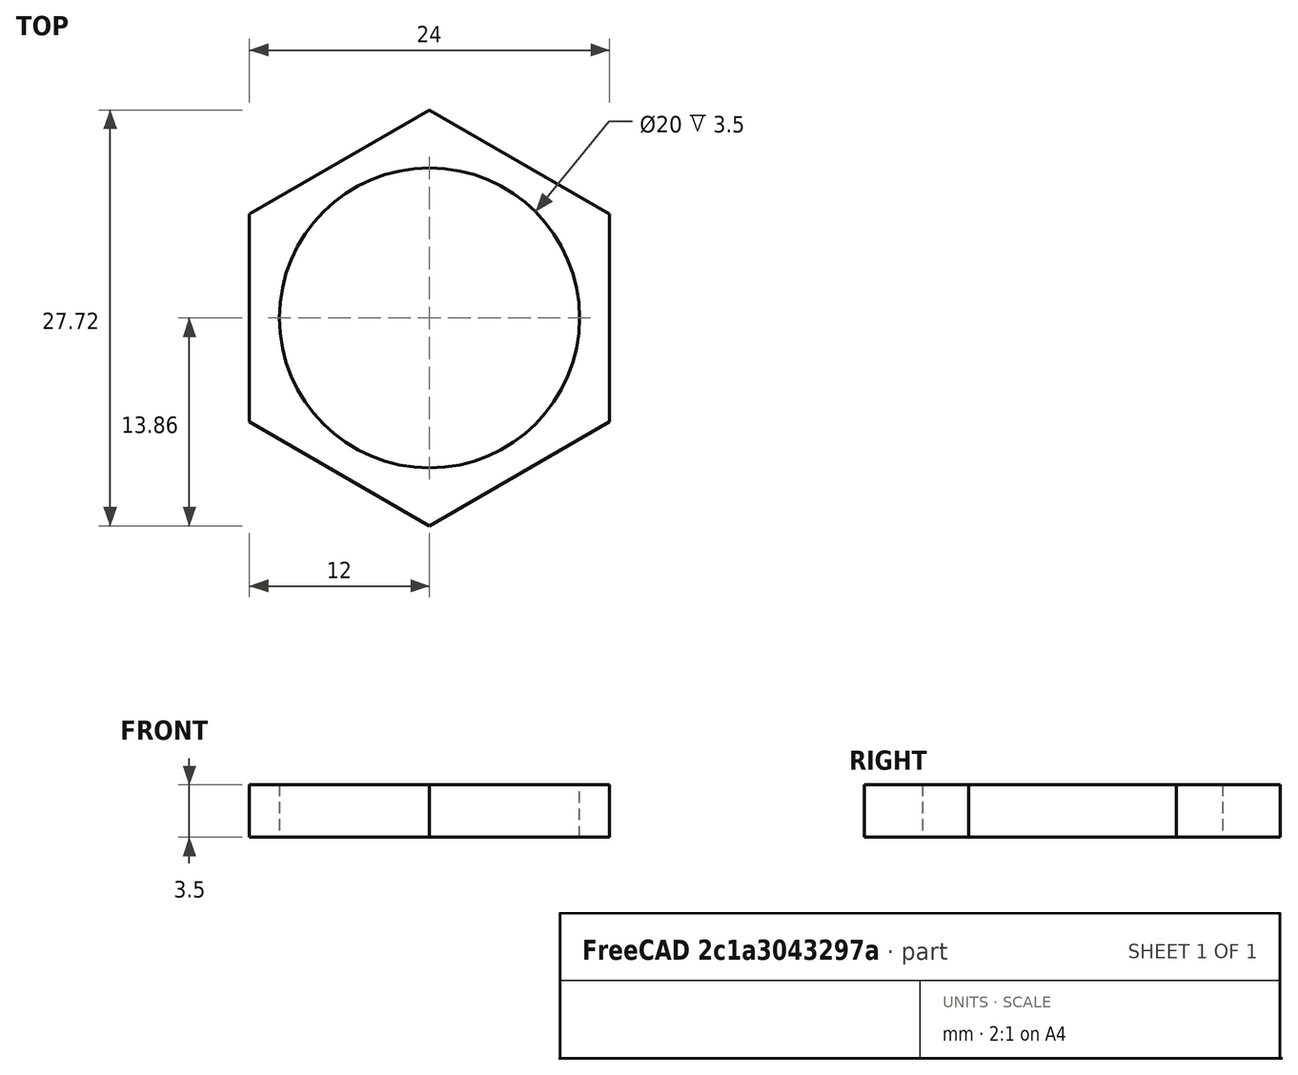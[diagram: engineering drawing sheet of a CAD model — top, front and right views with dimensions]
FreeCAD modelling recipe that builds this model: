
FCSTD DOCUMENT  (FreeCAD 0.14R3310 (Git))
Label: 33. TUERCA ARANDELA DE LA CERRADURA
License: CC-BY 3.0
LicenseURL: http://creativecommons.org/licenses/by/3.0/
objects: Sketcher::SketchObject×1, PartDesign::Pad×1
note: 3 computed .brp shape members not serialized (recipe doc carries the construction recipe); baked Part::Feature solids carry a one-line shape summary decoded from their .brp

FEATURE [Sketcher::SketchObject] Sketch
  sketch-geometry (7):
    g0: Circle CenterX=0 CenterY=0 CenterZ=0 NormalX=0 NormalY=0 NormalZ=1 Radius=10
    g1: LineSegment StartX=0 StartY=13.8564 StartZ=0 EndX=-12 EndY=6.9282 EndZ=0
    g2: LineSegment StartX=-12 StartY=6.9282 StartZ=0 EndX=-12 EndY=-6.9282 EndZ=0
    g3: LineSegment StartX=-12 StartY=-6.9282 StartZ=0 EndX=0 EndY=-13.8564 EndZ=0
    g4: LineSegment StartX=0 StartY=-13.8564 StartZ=0 EndX=12 EndY=-6.9282 EndZ=0
    g5: LineSegment StartX=12 StartY=-6.9282 StartZ=0 EndX=12 EndY=6.9282 EndZ=0
    g6: LineSegment StartX=12 StartY=6.9282 StartZ=0 EndX=0 EndY=13.8564 EndZ=0
  constraints (20):
    c: Radius(g0) = 10
    c: PointOnObject(g1,g-2)
    c: Coincident(g1,g2)
    c: Vertical(g2)
    c: Coincident(g2,g3)
    c: Coincident(g3,g4)
    c: Coincident(g4,g5)
    c: Vertical(g5)
    c: Coincident(g5,g6)
    c: Coincident(g6,g1)
    c: Equal(g5,g6)
    c: Equal(g6,g1)
    c: Equal(g1,g2)
    c: Equal(g2,g3)
    c: Equal(g3,g4)
    c: Symmetric(g1,g3,g-1)
    c: Angle(g2,g1) = 2.0944
    c: DistanceX(g-2,g4) = 12
    c: Symmetric(g4,g2,g-2)
    c: Coincident(g0,g-1)
FEATURE [PartDesign::Pad] Pad
  Length = 3.5
  Length2 = 100
  Sketch = -> Sketch
  Type = 0
